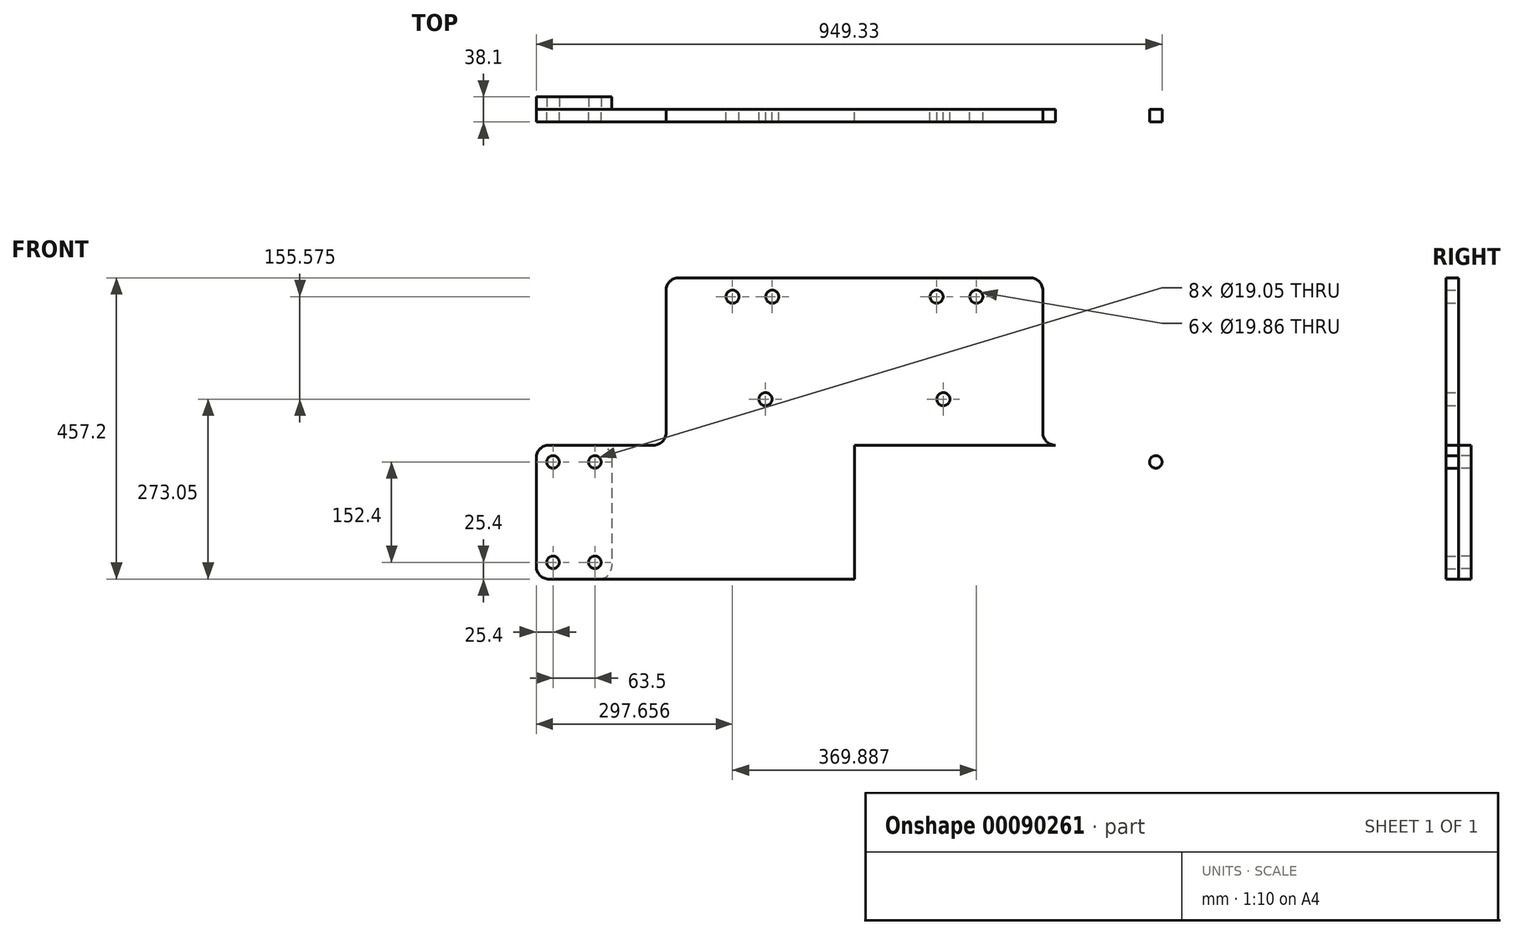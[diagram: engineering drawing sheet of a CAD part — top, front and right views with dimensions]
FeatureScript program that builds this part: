
annotation { "Feature Type Name" : "Feature", "Feature Type Description" : "" }
export const myFeature = defineFeature(function(context is Context, id is Id, definition is map)
    precondition{}
    {
        {
            var Q0;
            Q0=qCreatedBy(makeId("Front.planeOp"),FACE);
            var sketch = newSketch(context, id + "F0", { "sketchPlane" : qUnion([Q0])});
            skLineSegment(sketch, "E0", {"start": v(-285.75, -19.05) * mm, "end": v(-285.75, -234.95) * mm});
            skLineSegment(sketch, "E1", {"start": v(-304.8, -254) * mm, "end": v(-463.55, -254) * mm});
            skLineSegment(sketch, "E2", {"start": v(-482.6, -273.05) * mm, "end": v(-482.6, -438.15) * mm});
            skLineSegment(sketch, "E3", {"start": v(-463.55, -457.2) * mm, "end": v(0, -457.2) * mm});
            skLineSegment(sketch, "E4", {"start": v(0, -457.2) * mm, "end": v(0, 0) * mm});
            skLineSegment(sketch, "E5", {"start": v(0, 0) * mm, "end": v(-266.7, 0) * mm});
            skCircle(sketch, "E6", {"center": v(-184.94, -28.58) * mm, "radius": 9.93 * mm});
            skCircle(sketch, "E7", {"center": v(-124.62, -28.58) * mm, "radius": 9.93 * mm});
            skCircle(sketch, "E8", {"center": v(-134.94, -184.15) * mm, "radius": 9.93 * mm});
            skLineSegment(sketch, "E9", {"start": v(-285.75, -28.58) * mm, "end": v(0, -28.57) * mm, "construction": true});
            skCircle(sketch, "E10", {"center": v(-457.2, -279.4) * mm, "radius": 9.53 * mm});
            skCircle(sketch, "E11.0.1.0", {"center": v(-457.2, -431.8) * mm, "radius": 9.53 * mm});
            skCircle(sketch, "E11.1.0.0", {"center": v(-393.7, -279.4) * mm, "radius": 9.53 * mm});
            skCircle(sketch, "E11.1.1.0", {"center": v(-393.7, -431.8) * mm, "radius": 9.53 * mm});
            skLineSegment(sketch, "E11.direction1", {"start": v(-457.2, -279.4) * mm, "end": v(-393.7, -279.4) * mm, "construction": true});
            skLineSegment(sketch, "E11.direction2", {"start": v(-457.2, -279.4) * mm, "end": v(-457.2, -431.8) * mm, "construction": true});
            skCircle(sketch, "E12.MirrorC", {"center": v(457.2, -279.4) * mm, "radius": 9.53 * mm});
            skCircle(sketch, "E13.MirrorC", {"center": v(457.2, -431.8) * mm, "radius": 9.53 * mm});
            skCircle(sketch, "E14.MirrorC", {"center": v(393.7, -279.4) * mm, "radius": 9.53 * mm});
            skCircle(sketch, "E15.MirrorC", {"center": v(393.7, -431.8) * mm, "radius": 9.53 * mm});
            skCircle(sketch, "E16.MirrorC", {"center": v(184.94, -28.58) * mm, "radius": 9.93 * mm});
            skCircle(sketch, "E17.MirrorC", {"center": v(134.94, -184.15) * mm, "radius": 9.93 * mm});
            skCircle(sketch, "E18.MirrorC", {"center": v(124.62, -28.58) * mm, "radius": 9.93 * mm});
            skLineSegment(sketch, "E19.MirrorCS", {"start": v(463.55, -457.2) * mm, "end": v(0, -457.2) * mm});
            skLineSegment(sketch, "E20.MirrorCS", {"start": v(482.6, -273.05) * mm, "end": v(482.6, -438.15) * mm});
            skLineSegment(sketch, "E21.MirrorCS", {"start": v(285.75, -19.05) * mm, "end": v(285.75, -234.95) * mm});
            skLineSegment(sketch, "E22.MirrorCS", {"start": v(457.2, -279.4) * mm, "end": v(393.7, -279.4) * mm, "construction": true});
            skLineSegment(sketch, "E23.MirrorCS", {"start": v(304.8, -254) * mm, "end": v(463.55, -254) * mm});
            skLineSegment(sketch, "E24.MirrorCS", {"start": v(0, 0) * mm, "end": v(266.7, 0) * mm});
            skLineSegment(sketch, "E25.MirrorCS", {"start": v(285.75, -28.57) * mm, "end": v(0, -28.57) * mm, "construction": true});
            skLineSegment(sketch, "E26.MirrorCS", {"start": v(457.2, -279.4) * mm, "end": v(457.2, -431.8) * mm, "construction": true});
            skPoint(sketch, "E27.visualSharp", {"position": v(285.75, 0) * mm});
            skArc(sketch, "E27.filletArc", {"start": v(285.75, -19.05) * mm, "mid": v(280.17, -5.58) * mm, "end": v(266.7, 0) * mm});
            skPoint(sketch, "E28.visualSharp", {"position": v(285.75, -254) * mm});
            skArc(sketch, "E28.filletArc", {"start": v(285.75, -234.95) * mm, "mid": v(291.33, -248.42) * mm, "end": v(304.8, -254) * mm});
            skPoint(sketch, "E29.visualSharp", {"position": v(482.6, -254) * mm});
            skArc(sketch, "E29.filletArc", {"start": v(482.6, -273.05) * mm, "mid": v(477.02, -259.58) * mm, "end": v(463.55, -254) * mm});
            skPoint(sketch, "E30.visualSharp", {"position": v(482.6, -457.2) * mm});
            skArc(sketch, "E30.filletArc", {"start": v(463.55, -457.2) * mm, "mid": v(477.02, -451.62) * mm, "end": v(482.6, -438.15) * mm});
            skPoint(sketch, "E31.visualSharp", {"position": v(-482.6, -457.2) * mm});
            skArc(sketch, "E31.filletArc", {"start": v(-482.6, -438.15) * mm, "mid": v(-477.02, -451.62) * mm, "end": v(-463.55, -457.2) * mm});
            skPoint(sketch, "E32.visualSharp", {"position": v(-482.6, -254) * mm});
            skArc(sketch, "E32.filletArc", {"start": v(-463.55, -254) * mm, "mid": v(-477.02, -259.58) * mm, "end": v(-482.6, -273.05) * mm});
            skPoint(sketch, "E33.visualSharp", {"position": v(-285.75, -254) * mm});
            skArc(sketch, "E33.filletArc", {"start": v(-304.8, -254) * mm, "mid": v(-291.33, -248.42) * mm, "end": v(-285.75, -234.95) * mm});
            skPoint(sketch, "E34.visualSharp", {"position": v(-285.75, 0) * mm});
            skArc(sketch, "E34.filletArc", {"start": v(-266.7, 0) * mm, "mid": v(-280.17, -5.58) * mm, "end": v(-285.75, -19.05) * mm});
            skLineSegment(sketch, "E35", {"start": v(-304.8, -254) * mm, "end": v(304.8, -254) * mm});
            skSolve(sketch);
        }
        {
            var Q0;
            Q0=makeQuery(id+"F0.imprint","IMPRINT",FACE,{"disambiguationData":[TD([[makeQuery(id+"F0.imprint","IMPRINT",EDGE,{"derivedFrom":sQuery(id+"F0.wireOp",EDGE,"E4")}),-1.0]])]});
            var Q1;
            Q1=makeQuery(id+"F0.imprint","IMPRINT",FACE,{"disambiguationData":[TD([[makeQuery(id+"F0.imprint","IMPRINT",EDGE,{"derivedFrom":sQuery(id+"F0.wireOp",EDGE,"E0")}),1.0]])]});
            var Q2;
            {var subQ2=sQuery(id+"F0.wireOp",EDGE,"E1");Q2=makeQuery(id+"F0.imprint","IMPRINT",FACE,{"disambiguationData":[TD([[makeQuery(id+"F0.imprint","IMPRINT",EDGE,{"derivedFrom":subQ2}),1.0]])]});}
            var Q3;
            Q3=makeQuery(id+"F0.imprint","IMPRINT",FACE,{"disambiguationData":[TD([[makeQuery(id+"F0.imprint","IMPRINT",EDGE,{"derivedFrom":sQuery(id+"F0.wireOp",EDGE,"E12.MirrorC")}),1.0]])]});
            extrude(context, id + "F1", {"entities" : qUnion([Q0, Q1, Q2, Q3]), "depth" : 19.05 * mm});
        }
        {
            var Q0;
            Q0=qCreatedBy(makeId("Front.planeOp"),FACE);
            var sketch = newSketch(context, id + "F2", { "sketchPlane" : qUnion([Q0])});
            skLineSegment(sketch, "E36.0", {"start": v(-425.45, -254) * mm, "end": v(-463.55, -254) * mm});
            skLineSegment(sketch, "E36.1", {"start": v(-482.6, -273.05) * mm, "end": v(-482.6, -438.15) * mm});
            skArc(sketch, "E36.2", {"start": v(-463.55, -254) * mm, "mid": v(-477.02, -259.58) * mm, "end": v(-482.6, -273.05) * mm});
            skArc(sketch, "E36.3", {"start": v(-482.6, -438.15) * mm, "mid": v(-477.02, -451.62) * mm, "end": v(-463.55, -457.2) * mm});
            skLineSegment(sketch, "E36.4", {"start": v(-425.45, -457.2) * mm, "end": v(-463.55, -457.2) * mm});
            skCircle(sketch, "E36.5", {"center": v(-393.7, -431.8) * mm, "radius": 9.53 * mm});
            skCircle(sketch, "E36.6", {"center": v(-457.2, -431.8) * mm, "radius": 9.53 * mm});
            skCircle(sketch, "E36.7", {"center": v(-393.7, -279.4) * mm, "radius": 9.53 * mm});
            skCircle(sketch, "E36.8", {"center": v(-457.2, -279.4) * mm, "radius": 9.53 * mm});
            skPoint(sketch, "E37.newPointB", {"position": v(463.55, -457.2) * mm});
            skLineSegment(sketch, "E38", {"start": v(-457.2, -279.4) * mm, "end": v(-393.7, -279.4) * mm, "construction": true});
            skLineSegment(sketch, "E39", {"start": v(-457.2, -431.8) * mm, "end": v(-393.7, -431.8) * mm, "construction": true});
            skLineSegment(sketch, "E40", {"start": v(-425.45, -254) * mm, "end": v(-425.45, -457.2) * mm, "construction": true});
            skPoint(sketch, "E41.orphan", {"position": v(-425.45, -279.4) * mm});
            skPoint(sketch, "E42.orphan", {"position": v(-425.45, -431.8) * mm});
            skLineSegment(sketch, "E43.MirrorCS", {"start": v(-425.45, -254) * mm, "end": v(-387.35, -254) * mm});
            skArc(sketch, "E44.MirrorCS", {"start": v(-387.35, -254) * mm, "mid": v(-373.88, -259.58) * mm, "end": v(-368.3, -273.05) * mm});
            skLineSegment(sketch, "E45.MirrorCS", {"start": v(-368.3, -273.05) * mm, "end": v(-368.3, -438.15) * mm});
            skArc(sketch, "E46.MirrorCS", {"start": v(-368.3, -438.15) * mm, "mid": v(-373.88, -451.62) * mm, "end": v(-387.35, -457.2) * mm});
            skLineSegment(sketch, "E47.MirrorCS", {"start": v(-425.45, -457.2) * mm, "end": v(-387.35, -457.2) * mm});
            skSolve(sketch);
        }
        {
            var Q0;
            Q0 = qSketchRegion(id + "F2", true);
            extrude(context, id + "F3", {"entities" : qUnion([Q0]), "oppositeDirection" : true, "depth" : 19.05 * mm});
        }
    });
